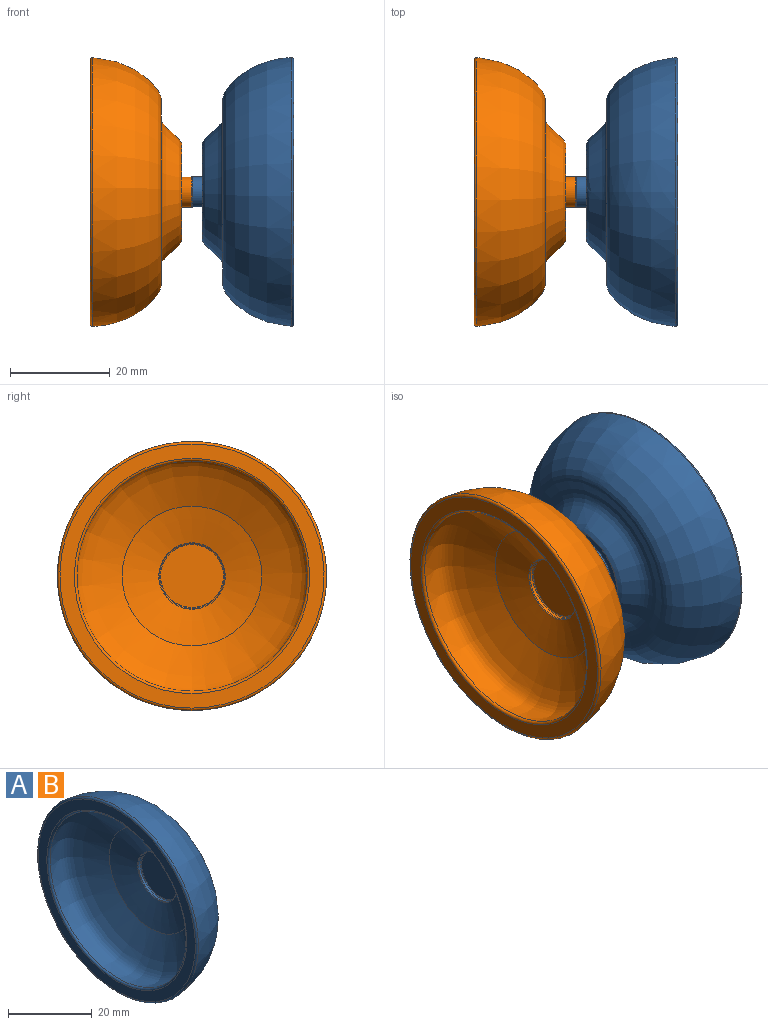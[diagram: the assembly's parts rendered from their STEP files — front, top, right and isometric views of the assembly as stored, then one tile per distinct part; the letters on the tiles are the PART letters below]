
ASSEMBLY  parts=2 mates=1
PART A: 28 faces, bbox 20.5x58.4x58.4 mm
  f0: plane 52.96x52.96mm, normal (-1,0,0), area 456.6mm2, adj f1,f27
  f1: torus R=23.57mm, axis (1,0,0), area 126.8mm2, adj f0,f2
  f2: revolved ~47.44x47.44mm, area 2121.2mm2, adj f1,f3
  f3: cone r=6.64mm half-angle=73.8deg, axis (-1,0,0), area 497.7mm2, adj f2,f4
  f4: torus R=6.7mm, axis (1,0,0), area 10.6mm2, adj f3,f5
  f5: cylinder r=6.5mm len=13mm, axis (1,0,0), area 26.5mm2, adj f4,f6
  f6: torus R=6.3mm, axis (1,0,0), area 12.7mm2, adj f5,f7
  f7: plane 12.6x12.6mm, normal (-1,0,0), area 124.7mm2, adj f6
  f8: plane 4.2x4.2mm, normal (1,0,0), area 13.9mm2, adj f9
  f9: cylinder r=2.1mm len=4.29mm, axis (1,0,0), area 56.6mm2, adj f8,f10
  f10: torus R=2.3mm, axis (1,0,0), area 4.3mm2, adj f9,f11
  f11: plane 5.8x5.8mm, normal (1,0,0), area 9.8mm2, adj f10,f12
  f12: torus R=2.9mm, axis (1,0,0), area 6mm2, adj f11,f13
  f13: cylinder r=3.1mm len=6.2mm, axis (1,0,0), area 40.9mm2, adj f12,f14
  f14: plane 7.8x7.8mm, normal (1,0,0), area 17.6mm2, adj f13,f15
  f15: torus R=3.9mm, axis (1,0,0), area 7.9mm2, adj f14,f16
  f16: cylinder r=4.1mm len=8.2mm, axis (1,0,0), area 15.5mm2, adj f15,f17
  f17: torus R=4.3mm, axis (1,0,0), area 8.2mm2, adj f16,f18
  f18: plane 12.51x12.51mm, normal (1,0,0), area 64.8mm2, adj f17,f19
  f19: torus R=6.25mm, axis (1,0,0), area 12.4mm2, adj f18,f20
  f20: cone r=6.45mm half-angle=1.6deg, axis (1,0,0), area 38.8mm2, adj f19,f21
  f21: plane 14x14mm, normal (1,0,0), area 22mm2, adj f20,f22
  f22: cylinder r=7mm len=14mm, axis (1,0,0), area 44mm2, adj f21,f23
  f23: plane 19x19mm, normal (1,0,0), area 129.6mm2, adj f22,f24
  f24: cone r=9.5mm half-angle=0deg, axis (1,0,0), area 47.4mm2, adj f23,f25
  f25: torus R=9.7mm, axis (1,0,0), area 19.6mm2, adj f24,f26
  f26: revolved ~53.95x53.95mm, area 3495.1mm2, adj f25,f27
  f27: torus R=26.48mm, axis (1,0,0), area 137mm2, adj f0,f26
PART B: same geometry as A
PLACE A rot(axis=(0,-1,0),180deg) t=(103.76,-3.91,-8.55)mm
PLACE B t=(-102.95,-3.91,10.29)mm
MATE planar B.f10 <-> A.f10  axis (1,0,0) through (0.31,-3.91,0.87)mm
